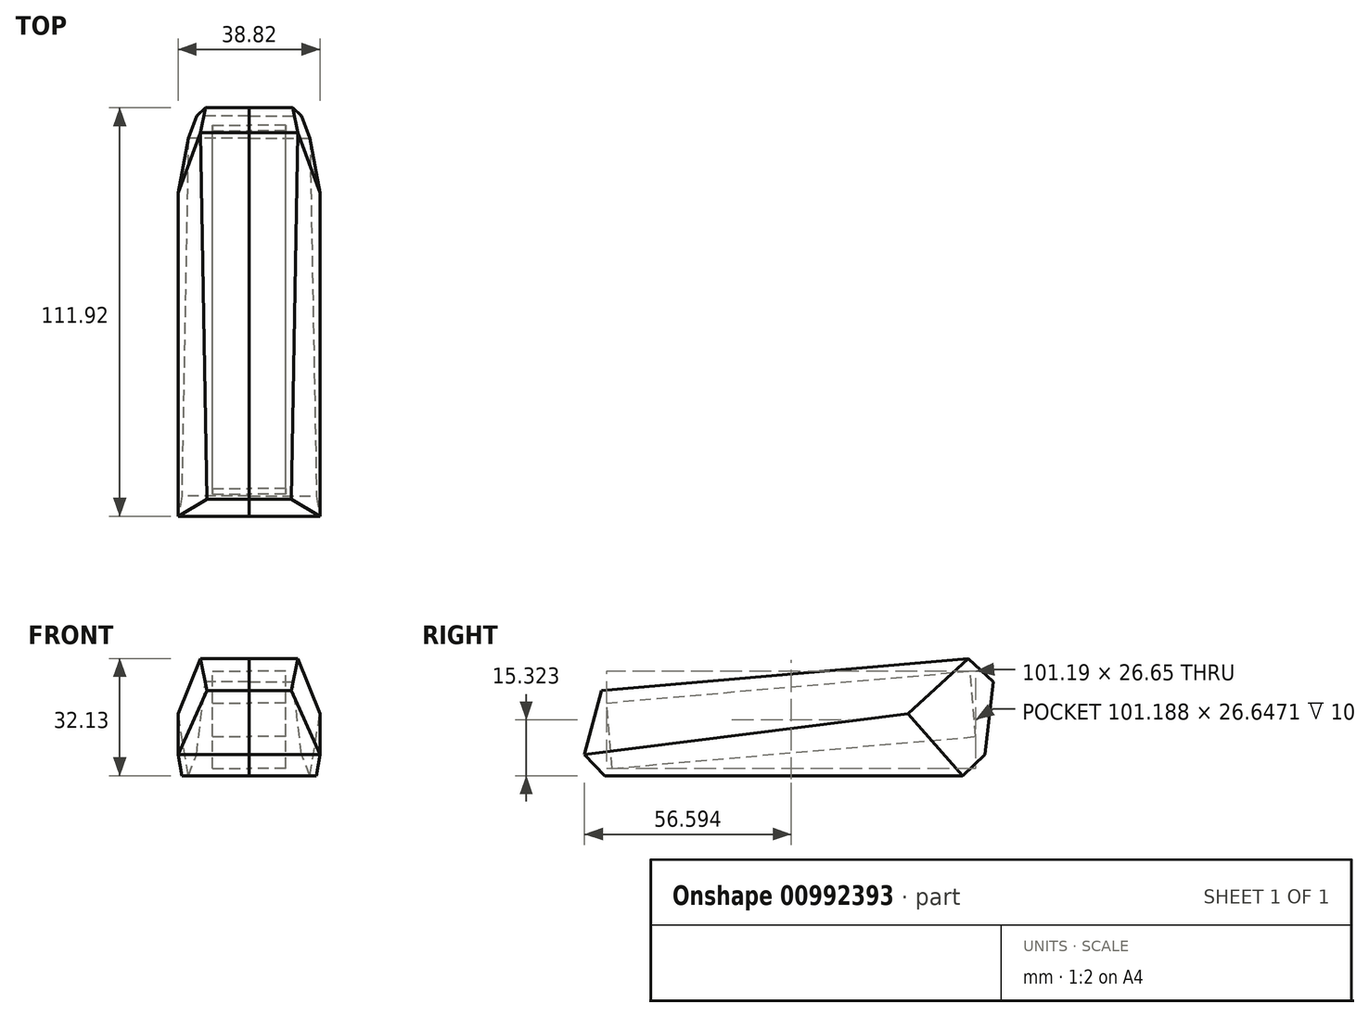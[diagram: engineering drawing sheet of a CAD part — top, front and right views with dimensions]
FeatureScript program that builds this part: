
annotation { "Feature Type Name" : "Feature", "Feature Type Description" : "" }
export const myFeature = defineFeature(function(context is Context, id is Id, definition is map)
    precondition{}
    {
        {
            var Q0;
            Q0=qCreatedBy(makeId("Right.planeOp"),FACE);
            var sketch = newSketch(context, id + "F0", { "sketchPlane" : qUnion([Q0])});
            skLineSegment(sketch, "E0.bottom", {"start": v(0, 0) * mm, "end": v(115, 0) * mm});
            skLineSegment(sketch, "E0.top", {"start": v(0, 33) * mm, "end": v(115, 33) * mm});
            skLineSegment(sketch, "E0.left", {"start": v(0, 0) * mm, "end": v(0, 33) * mm});
            skLineSegment(sketch, "E0.right", {"start": v(115, 0) * mm, "end": v(115, 33) * mm});
            skSolve(sketch);
        }
        {
            var Q0;
            Q0 = qSketchRegion(id + "F0", true);
            extrude(context, id + "F1", {"entities" : qUnion([Q0]), "oppositeDirection" : true, "depth" : 25 * mm, "offsetDistance" : 25 * mm});
        }
        {
            var Q0;
            Q0=makeQuery(id+"F1.opExtrude","CAP_FACE",FACE,{"disambiguationData":[OSD([sQuery(id+"F0.wireOp",EDGE,"E0.bottom"),sQuery(id+"F0.wireOp",EDGE,"E0.top"),sQuery(id+"F0.wireOp",EDGE,"E0.left"),sQuery(id+"F0.wireOp",EDGE,"E0.right")])],"isStart":true});
            var sketch = newSketch(context, id + "F2", { "sketchPlane" : qUnion([Q0])});
            skLineSegment(sketch, "E1.0", {"start": v(6, 19.93) * mm, "end": v(105.62, 28.65) * mm});
            skLineSegment(sketch, "E1.1", {"start": v(7.57, 2) * mm, "end": v(6, 19.93) * mm});
            skLineSegment(sketch, "E1.2", {"start": v(7.57, 2) * mm, "end": v(107.19, 10.72) * mm});
            skLineSegment(sketch, "E1.3", {"start": v(107.19, 10.72) * mm, "end": v(105.62, 28.65) * mm});
            skLineSegment(sketch, "E2", {"start": v(0, 0) * mm, "end": v(248.04, 21.7) * mm, "construction": true});
            skSolve(sketch);
        }
        {
            var Q0;
            Q0 = qSketchRegion(id + "F2", true);
            extrude(context, id + "F3", {"entities" : qUnion([Q0]), "operationType" : NewBodyOperationType.REMOVE, "oppositeDirection" : true, "depth" : 10 * mm, "offsetDistance" : 25 * mm});
        }
        {
            var Q0;
            Q0=makeQuery(id+"F1.opExtrude","CAP_FACE",FACE,{"disambiguationData":[OSD([sQuery(id+"F0.wireOp",EDGE,"E0.bottom"),sQuery(id+"F0.wireOp",EDGE,"E0.top"),sQuery(id+"F0.wireOp",EDGE,"E0.left"),sQuery(id+"F0.wireOp",EDGE,"E0.right")])],"isStart":false});
            var sketch = newSketch(context, id + "F4", { "sketchPlane" : qUnion([Q0])});
            skLineSegment(sketch, "E3", {"start": v(-5.47, 0) * mm, "end": v(0, 5.83) * mm});
            skLineSegment(sketch, "E4", {"start": v(0, 5.83) * mm, "end": v(-7.22, 33) * mm});
            skLineSegment(sketch, "E5", {"start": v(-7.22, 33) * mm, "end": v(-7.22, 35.82) * mm});
            skLineSegment(sketch, "E6", {"start": v(-7.22, 35.82) * mm, "end": v(5.38, 35.82) * mm});
            skLineSegment(sketch, "E7", {"start": v(5.38, 35.82) * mm, "end": v(5.38, -11.15) * mm});
            skLineSegment(sketch, "E8", {"start": v(5.38, -11.15) * mm, "end": v(-7.22, -11.15) * mm});
            skLineSegment(sketch, "E9", {"start": v(-7.22, -11.15) * mm, "end": v(-5.47, 0) * mm});
            skSolve(sketch);
        }
        {
            var Q0;
            Q0 = qSketchRegion(id + "F4", true);
            extrude(context, id + "F5", {"entities" : qUnion([Q0]), "operationType" : NewBodyOperationType.REMOVE, "oppositeDirection" : true, "depth" : 25 * mm, "offsetDistance" : 25 * mm});
        }
        {
            var Q0;
            Q0=makeQuery(id+"F1.opExtrude","CAP_FACE",FACE,{"disambiguationData":[OSD([sQuery(id+"F0.wireOp",EDGE,"E0.bottom"),sQuery(id+"F0.wireOp",EDGE,"E0.top"),sQuery(id+"F0.wireOp",EDGE,"E0.left"),sQuery(id+"F0.wireOp",EDGE,"E0.right")])],"isStart":false});
            var sketch = newSketch(context, id + "F6", { "sketchPlane" : qUnion([Q0])});
            skLineSegment(sketch, "E10", {"start": v(0, 0) * mm, "end": v(-102.91, 9) * mm, "construction": true});
            skLineSegment(sketch, "E11", {"start": v(-4.65, 23.35) * mm, "end": v(-115, 33) * mm});
            skLineSegment(sketch, "E12", {"start": v(-115, 33) * mm, "end": v(-115, 36.12) * mm});
            skLineSegment(sketch, "E13", {"start": v(-115, 36.12) * mm, "end": v(-3.68, 36.12) * mm});
            skLineSegment(sketch, "E14", {"start": v(-3.68, 36.12) * mm, "end": v(-4.65, 23.35) * mm});
            skSolve(sketch);
        }
        {
            var Q0;
            Q0 = qSketchRegion(id + "F6", true);
            extrude(context, id + "F7", {"entities" : qUnion([Q0]), "operationType" : NewBodyOperationType.REMOVE, "oppositeDirection" : true, "depth" : 25 * mm, "offsetDistance" : 25 * mm});
        }
        {
            var Q0;
            Q0=makeQuery(id+"F1.opExtrude","CAP_FACE",FACE,{"disambiguationData":[OSD([sQuery(id+"F0.wireOp",EDGE,"E0.bottom"),sQuery(id+"F0.wireOp",EDGE,"E0.top"),sQuery(id+"F0.wireOp",EDGE,"E0.left"),sQuery(id+"F0.wireOp",EDGE,"E0.right")])],"isStart":false});
            var sketch = newSketch(context, id + "F8", { "sketchPlane" : qUnion([Q0])});
            skLineSegment(sketch, "E15", {"start": v(-105.06, 32.13) * mm, "end": v(-111.92, 25.73) * mm});
            skLineSegment(sketch, "E16", {"start": v(-111.92, 25.73) * mm, "end": v(-109.65, 5.83) * mm});
            skLineSegment(sketch, "E17", {"start": v(-121.24, -0.43) * mm, "end": v(-121.24, 36.3) * mm});
            skLineSegment(sketch, "E18", {"start": v(-121.24, 36.3) * mm, "end": v(-105.06, 32.13) * mm});
            skLineSegment(sketch, "E19", {"start": v(-109.65, 5.83) * mm, "end": v(-103.55, 0) * mm});
            skLineSegment(sketch, "E20", {"start": v(-103.55, 0) * mm, "end": v(-103.55, -4.01) * mm});
            skLineSegment(sketch, "E21", {"start": v(-103.55, -4.01) * mm, "end": v(-121.24, -0.43) * mm});
            skSolve(sketch);
        }
        {
            var Q0;
            Q0 = qSketchRegion(id + "F8", true);
            extrude(context, id + "F9", {"entities" : qUnion([Q0]), "operationType" : NewBodyOperationType.REMOVE, "oppositeDirection" : true, "depth" : 25 * mm, "offsetDistance" : 25 * mm});
        }
        {
            var Q0;
            Q0=qCreatedBy(makeId("Front.planeOp"),FACE);
            var sketch = newSketch(context, id + "F10", { "sketchPlane" : qUnion([Q0])});
            skLineSegment(sketch, "E22", {"start": v(-16.23, -16.01) * mm, "end": v(-19.41, 5.83) * mm});
            skLineSegment(sketch, "E23", {"start": v(-12.15, 37.14) * mm, "end": v(-31.83, 37.14) * mm});
            skLineSegment(sketch, "E24", {"start": v(-31.83, 37.14) * mm, "end": v(-30.66, -5.7) * mm});
            skLineSegment(sketch, "E25", {"start": v(-16.23, -16.01) * mm, "end": v(-17.22, -18.88) * mm});
            skLineSegment(sketch, "E26", {"start": v(-17.22, -18.88) * mm, "end": v(-33.57, -19.33) * mm});
            skLineSegment(sketch, "E27", {"start": v(-33.57, -19.33) * mm, "end": v(-30.66, -5.7) * mm});
            skLineSegment(sketch, "E28", {"start": v(-19.41, 5.83) * mm, "end": v(-9, 28.23) * mm});
            skLineSegment(sketch, "E29", {"start": v(-9, 28.23) * mm, "end": v(-7.78, 35.44) * mm});
            skLineSegment(sketch, "E30", {"start": v(-7.78, 35.44) * mm, "end": v(-12.15, 37.14) * mm});
            skSolve(sketch);
        }
        {
            var Q0;
            Q0=makeQuery(id+"F1.opExtrude","CAP_FACE",FACE,{"disambiguationData":[OSD([sQuery(id+"F0.wireOp",EDGE,"E0.bottom"),sQuery(id+"F0.wireOp",EDGE,"E0.top"),sQuery(id+"F0.wireOp",EDGE,"E0.left"),sQuery(id+"F0.wireOp",EDGE,"E0.right")])],"isStart":false});
            var sketch = newSketch(context, id + "F11", { "sketchPlane" : qUnion([Q0])});
            skLineSegment(sketch, "E31", {"start": v(0, 5.83) * mm, "end": v(-123.26, 21.33) * mm});
            skSolve(sketch);
        }
        {
            var Q0;
            Q0=makeQuery(id+"F10.imprint","IMPRINT",FACE,{"disambiguationData":[TD([[makeQuery(id+"F10.imprint","IMPRINT",EDGE,{"derivedFrom":sQuery(id+"F10.wireOp",EDGE,"E22")}),1.0]])]});
            var Q1;
            Q1 = qConstructionFilter(qBodyType(qCreatedBy(id + "F11" ,EDGE), BodyType.WIRE), ConstructionObject.NO);
            sweep(context, id + "F12", {"operationType" : NewBodyOperationType.REMOVE, "profiles" : qUnion([Q0]), "path" : qUnion([Q1])});
        }
        {
            var Q0;
            Q0=qCreatedBy(makeId("Top.planeOp"),FACE);
            var sketch = newSketch(context, id + "F13", { "sketchPlane" : qUnion([Q0])});
            skLineSegment(sketch, "E32", {"start": v(-13.4, 117.59) * mm, "end": v(-22.04, 80.5) * mm});
            skLineSegment(sketch, "E33", {"start": v(-22.04, 80.5) * mm, "end": v(-24.18, 114.23) * mm});
            skLineSegment(sketch, "E34", {"start": v(-24.18, 114.23) * mm, "end": v(-13.4, 117.59) * mm});
            skSolve(sketch);
        }
        {
            var Q0;
            Q0=qCreatedBy(makeId("Front.planeOp"),FACE);
            cPlane(context, id + "F14", {"entities" : qUnion([Q0]), "cplaneType" : CPlaneType.OFFSET, "offset" : 88.6 * mm, "oppositeDirection" : true, "width" : 150 * mm, "height" : 150 * mm});
        }
        {
            var Q0;
            Q0=qCreatedBy(id+"F14.planeOp",FACE);
            var sketch = newSketch(context, id + "F15", { "sketchPlane" : qUnion([Q0])});
            skPoint(sketch, "E35", {"position": v(-19.41, 16.98) * mm});
            skSolve(sketch);
        }
        {
            var Q0;
            Q0=makeQuery(id+"F12.boolean.opBoolean","INTERSECT",VERTEX,{"derivedFrom":[makeQuery(id+"F9.boolean.opBoolean","COPY",FACE,{"derivedFrom":makeQuery(id+"F9.opExtrude","SWEPT_FACE",FACE,{"disambiguationData":[OSD([sQuery(id+"F8.wireOp",EDGE,"E19")])]})}),makeQuery(id+"F1.opExtrude","SWEPT_FACE",FACE,{"disambiguationData":[OSD([sQuery(id+"F0.wireOp",EDGE,"E0.bottom")])]}),makeQuery(id+"F12.opSweep","SWEPT_FACE",FACE,{"disambiguationData":[OSD([sQuery(id+"F10.wireOp",EDGE,"E22"),sQuery(id+"F11.wireOp",EDGE,"E31")])]})]});
            var Q1;
            Q1=makeQuery(id+"F12.boolean.opBoolean","INTERSECT",VERTEX,{"derivedFrom":[makeQuery(id+"F9.boolean.opBoolean","COPY",FACE,{"derivedFrom":makeQuery(id+"F9.opExtrude","SWEPT_FACE",FACE,{"disambiguationData":[OSD([sQuery(id+"F8.wireOp",EDGE,"E15")])]})}),makeQuery(id+"F7.boolean.opBoolean","COPY",FACE,{"derivedFrom":makeQuery(id+"F7.opExtrude","SWEPT_FACE",FACE,{"disambiguationData":[OSD([sQuery(id+"F6.wireOp",EDGE,"E11")])]})}),makeQuery(id+"F12.opSweep","SWEPT_FACE",FACE,{"disambiguationData":[OSD([sQuery(id+"F10.wireOp",EDGE,"E28"),sQuery(id+"F11.wireOp",EDGE,"E31")])]})]});
            var Q2;
            Q2=sQuery(id+"F15.wireOp",VERTEX,"E35");
            cPlane(context, id + "F16", {"entities" : qUnion([Q0, Q1, Q2]), "cplaneType" : CPlaneType.THREE_POINT, "offset" : 25 * mm, "width" : 150 * mm, "height" : 150 * mm});
        }
        {
            var Q0;
            Q0=qCreatedBy(id+"F16.planeOp",FACE);
            var sketch = newSketch(context, id + "F17", { "sketchPlane" : qUnion([Q0])});
            skLineSegment(sketch, "E36.bottom", {"start": v(-108.16, 33.49) * mm, "end": v(-75.36, 33.49) * mm});
            skLineSegment(sketch, "E36.top", {"start": v(-108.16, -4.48) * mm, "end": v(-75.36, -4.48) * mm});
            skLineSegment(sketch, "E36.left", {"start": v(-108.16, 33.49) * mm, "end": v(-108.16, -4.48) * mm});
            skLineSegment(sketch, "E36.right", {"start": v(-75.36, 33.49) * mm, "end": v(-75.36, -4.48) * mm});
            skSolve(sketch);
        }
        {
            var Q0;
            Q0 = qSketchRegion(id + "F17", true);
            extrude(context, id + "F18", {"entities" : qUnion([Q0]), "operationType" : NewBodyOperationType.REMOVE, "depth" : 25 * mm, "offsetDistance" : 25 * mm});
        }
        {
            var Q0;
            Q0=makeQuery(id+"F1.opExtrude","SWEPT_BODY",BODY,{"disambiguationData":[OSD([sQuery(id+"F0.wireOp",EDGE,"E0.bottom"),sQuery(id+"F0.wireOp",EDGE,"E0.top"),sQuery(id+"F0.wireOp",EDGE,"E0.left"),sQuery(id+"F0.wireOp",EDGE,"E0.right")])]});
            var Q1;
            Q1=qCreatedBy(makeId("Right.planeOp"),FACE);
            mirror(context, id + "F19", {"entities" : qUnion([Q0]), "mirrorPlane" : qUnion([Q1])});
        }
    });
